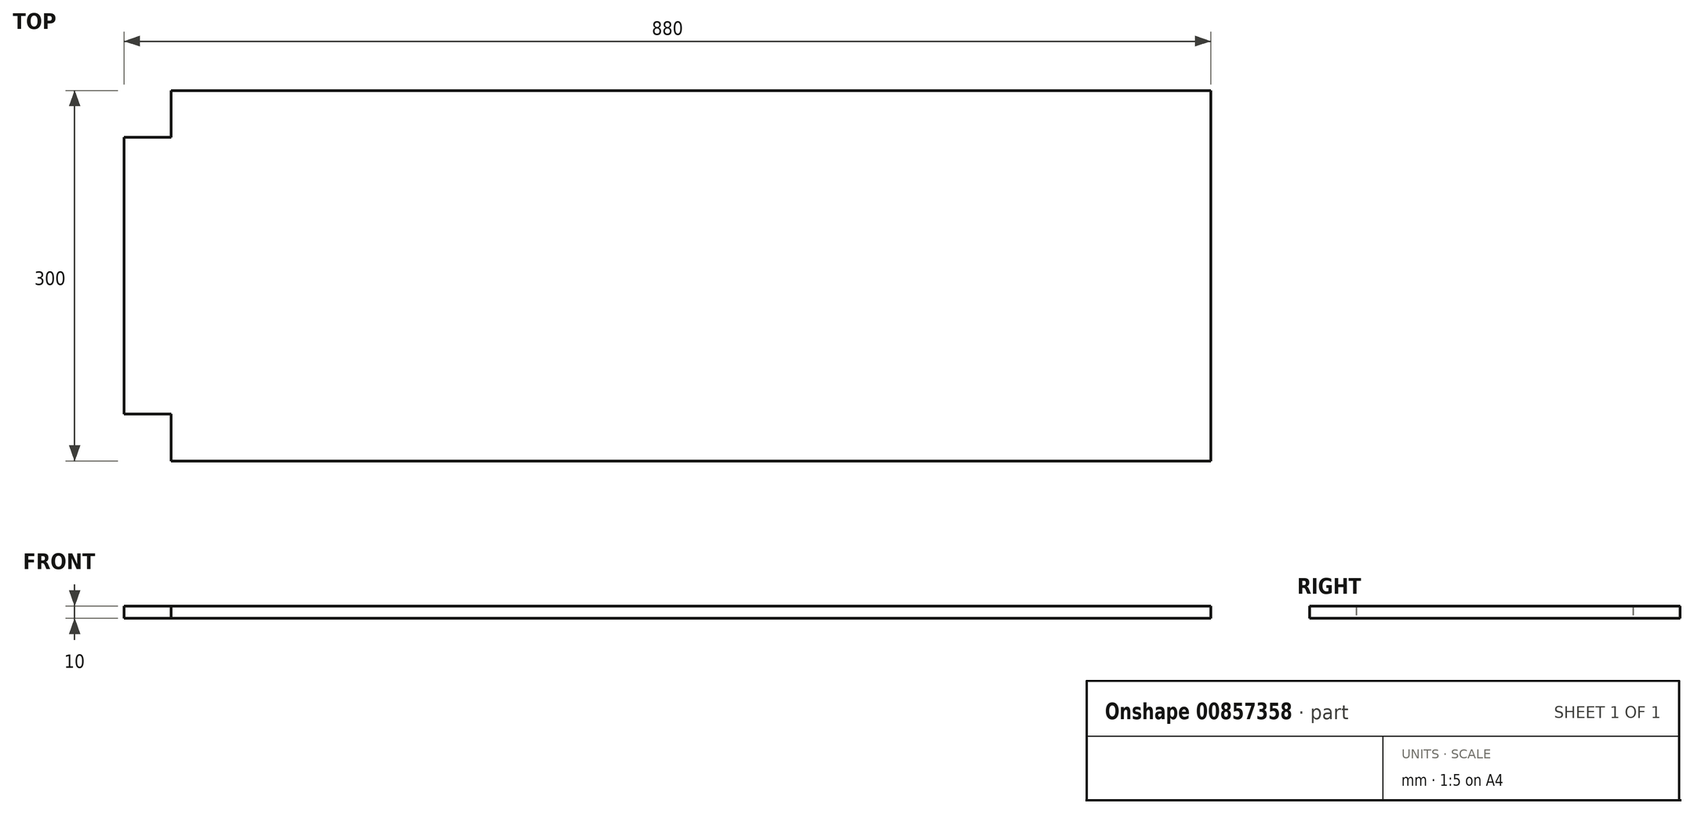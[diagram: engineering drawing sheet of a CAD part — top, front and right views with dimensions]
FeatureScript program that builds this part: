
annotation { "Feature Type Name" : "Feature", "Feature Type Description" : "" }
export const myFeature = defineFeature(function(context is Context, id is Id, definition is map)
    precondition{}
    {
        {
            var Q0;
            Q0=qCreatedBy(makeId("Top.planeOp"),FACE);
            var sketch = newSketch(context, id + "F0", { "sketchPlane" : qUnion([Q0])});
            skLineSegment(sketch, "E0.bottom", {"start": v(-796.3, 288.57) * mm, "end": v(45.7, 288.57) * mm});
            skLineSegment(sketch, "E0.top", {"start": v(-796.3, -11.43) * mm, "end": v(45.7, -11.43) * mm});
            skLineSegment(sketch, "E0.left", {"start": v(-796.3, 288.57) * mm, "end": v(-796.3, 250.57) * mm});
            skLineSegment(sketch, "E0.right", {"start": v(45.7, 288.57) * mm, "end": v(45.7, -11.43) * mm});
            skLineSegment(sketch, "E1", {"start": v(-796.3, 26.57) * mm, "end": v(-834.3, 26.57) * mm});
            skLineSegment(sketch, "E2", {"start": v(-834.3, 26.57) * mm, "end": v(-834.3, 250.57) * mm});
            skLineSegment(sketch, "E3", {"start": v(-834.3, 250.57) * mm, "end": v(-796.3, 250.57) * mm});
            skLineSegment(sketch, "E4.trimOffspring", {"start": v(-796.3, 26.57) * mm, "end": v(-796.3, -11.43) * mm});
            skSolve(sketch);
        }
        {
            var Q0;
            Q0=makeQuery(id+"F0.imprint","IMPRINT",FACE,{"disambiguationData":[TD([[makeQuery(id+"F0.imprint","IMPRINT",EDGE,{"derivedFrom":sQuery(id+"F0.wireOp",EDGE,"E0.bottom")}),-1.0]])]});
            extrude(context, id + "F1", {"entities" : qUnion([Q0]), "depth" : 10 * mm, "offsetDistance" : 25 * mm});
        }
    });
